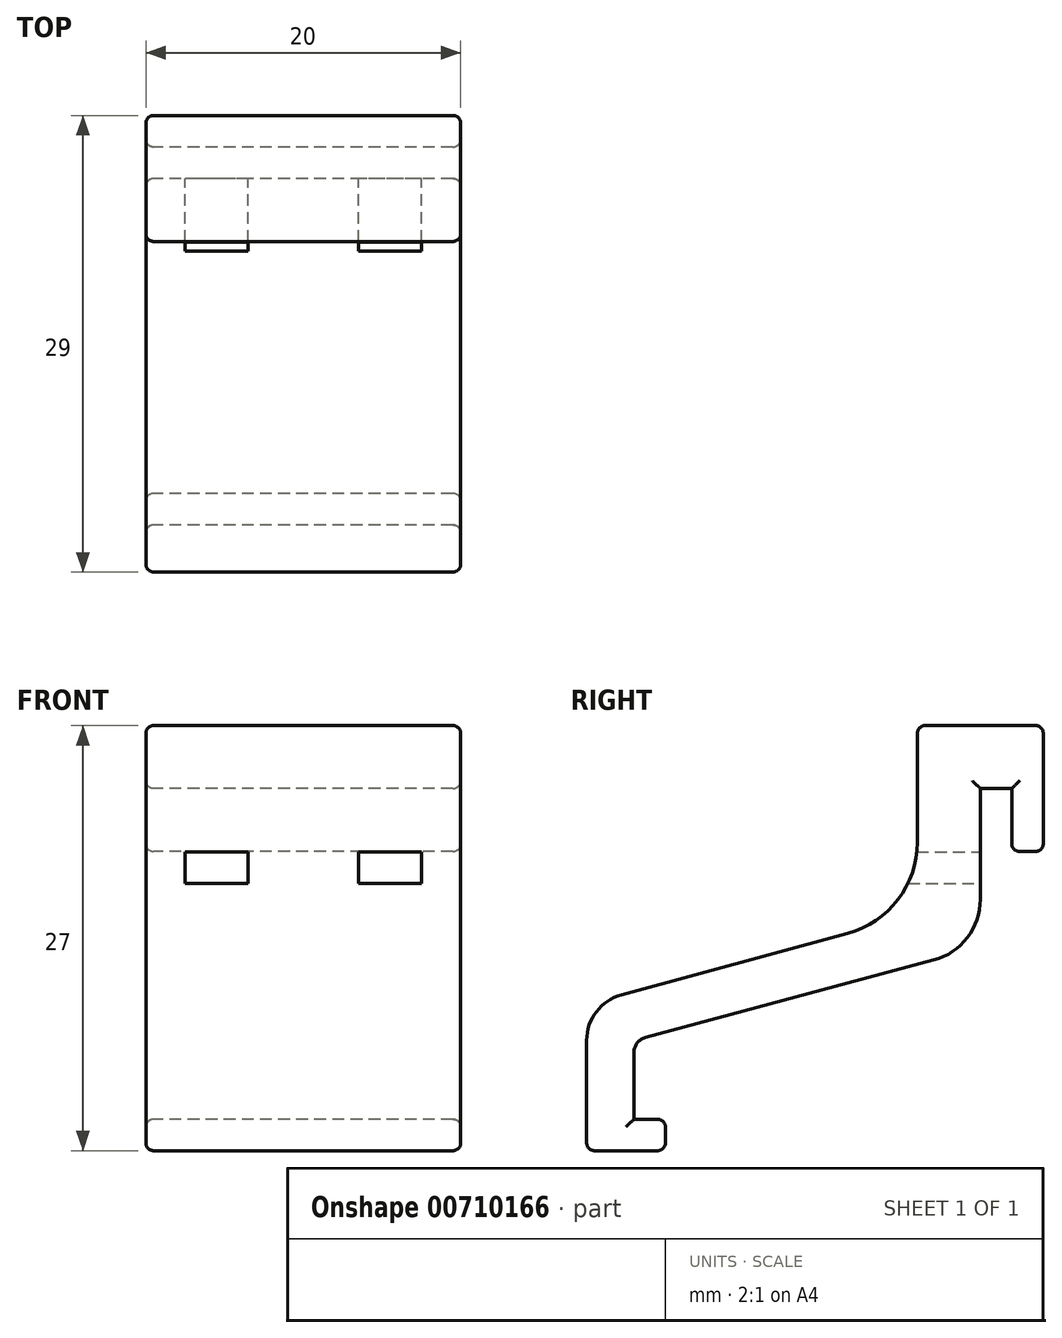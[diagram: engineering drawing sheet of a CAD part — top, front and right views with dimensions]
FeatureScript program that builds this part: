
annotation { "Feature Type Name" : "Feature", "Feature Type Description" : "" }
export const myFeature = defineFeature(function(context is Context, id is Id, definition is map)
    precondition{}
    {
        {
            var Q0;
            Q0=qCreatedBy(makeId("Right.planeOp"),FACE);
            var sketch = newSketch(context, id + "F0", { "sketchPlane" : qUnion([Q0])});
            skLineSegment(sketch, "E0.left", {"start": v(0, 0) * mm, "end": v(0, -7.04) * mm});
            skLineSegment(sketch, "E0.right", {"start": v(-4, 0) * mm, "end": v(-4, -3.41) * mm});
            skLineSegment(sketch, "E1.bottom", {"start": v(0, 0) * mm, "end": v(2, 0) * mm});
            skLineSegment(sketch, "E1.top", {"start": v(-4, 4) * mm, "end": v(4, 4) * mm});
            skLineSegment(sketch, "E1.left", {"start": v(-4, 0) * mm, "end": v(-4, 4) * mm});
            skLineSegment(sketch, "E1.right", {"start": v(4, 0) * mm, "end": v(4, 4) * mm});
            skLineSegment(sketch, "E2.top", {"start": v(4, -4) * mm, "end": v(2, -4) * mm});
            skLineSegment(sketch, "E2.left", {"start": v(4, 0) * mm, "end": v(4, -4) * mm});
            skLineSegment(sketch, "E2.right", {"start": v(2, 0) * mm, "end": v(2, -4) * mm});
            skLineSegment(sketch, "E3", {"start": v(-4, -16) * mm, "end": v(-43.7, -16) * mm, "construction": true});
            skLineSegment(sketch, "E4", {"start": v(-25, 0) * mm, "end": v(-25, -25.14) * mm, "construction": true});
            skLineSegment(sketch, "E5.bottom", {"start": v(-25, -16) * mm, "end": v(-22, -16) * mm});
            skLineSegment(sketch, "E5.left", {"start": v(-25, -16) * mm, "end": v(-25, -21) * mm});
            skLineSegment(sketch, "E5.right", {"start": v(-22, -16.77) * mm, "end": v(-22, -21) * mm});
            skLineSegment(sketch, "E6.bottom", {"start": v(-22, -21) * mm, "end": v(-20, -21) * mm});
            skLineSegment(sketch, "E6.top", {"start": v(-25, -23) * mm, "end": v(-20, -23) * mm});
            skLineSegment(sketch, "E6.left", {"start": v(-25, -21) * mm, "end": v(-25, -23) * mm});
            skLineSegment(sketch, "E6.right", {"start": v(-20, -21) * mm, "end": v(-20, -23) * mm});
            skArc(sketch, "E7", {"start": v(-22.79, -13.1) * mm, "mid": v(-24.38, -14.18) * mm, "end": v(-25, -16) * mm});
            skLineSegment(sketch, "E8", {"start": v(-21.26, -15.8) * mm, "end": v(-2.96, -10.9) * mm});
            skLineSegment(sketch, "E9", {"start": v(-8.43, -9.2) * mm, "end": v(-22.79, -13.1) * mm});
            skPoint(sketch, "E10.orphan", {"position": v(0, -16) * mm});
            skPoint(sketch, "E11.visualSharp", {"position": v(-4, -8) * mm});
            skArc(sketch, "E11.filletArc", {"start": v(-8.43, -9.2) * mm, "mid": v(-5.23, -7.06) * mm, "end": v(-4, -3.41) * mm});
            skPoint(sketch, "E12.visualSharp", {"position": v(0, -10.1) * mm});
            skArc(sketch, "E12.filletArc", {"start": v(-2.96, -10.9) * mm, "mid": v(-0.83, -9.47) * mm, "end": v(0, -7.04) * mm});
            skArc(sketch, "E13.filletArc", {"start": v(-21.26, -15.8) * mm, "mid": v(-21.8, -16.16) * mm, "end": v(-22, -16.77) * mm});
            skSolve(sketch);
        }
        {
            var Q0;
            Q0=makeQuery(id+"F0.imprint","IMPRINT",FACE,{"disambiguationData":[TD([[makeQuery(id+"F0.imprint","IMPRINT",EDGE,{"derivedFrom":sQuery(id+"F0.wireOp",EDGE,"E0.left")}),-1.0]])]});
            extrude(context, id + "F1", {"entities" : qUnion([Q0]), "endBound" : BoundingType.SYMMETRIC, "depth" : 20 * mm, "offsetDistance" : 25 * mm});
        }
        {
            var Q0;
            Q0=makeQuery(id+"F1.opExtrude","SWEPT_FACE",FACE,{"disambiguationData":[OSD([sQuery(id+"F0.wireOp",EDGE,"E0.left")])]});
            var sketch = newSketch(context, id + "F2", { "sketchPlane" : qUnion([Q0])});
            skLineSegment(sketch, "E14.bottom", {"start": v(-7.5, -6.02) * mm, "end": v(-3.5, -6.02) * mm});
            skLineSegment(sketch, "E14.top", {"start": v(-7.5, -4.02) * mm, "end": v(-3.5, -4.02) * mm});
            skLineSegment(sketch, "E14.left", {"start": v(-7.5, -6.02) * mm, "end": v(-7.5, -4.02) * mm});
            skLineSegment(sketch, "E14.right", {"start": v(-3.5, -6.02) * mm, "end": v(-3.5, -4.02) * mm});
            skLineSegment(sketch, "E15.bottom", {"start": v(3.5, -6.02) * mm, "end": v(7.5, -6.02) * mm});
            skLineSegment(sketch, "E15.top", {"start": v(3.5, -4.02) * mm, "end": v(7.5, -4.02) * mm});
            skLineSegment(sketch, "E15.left", {"start": v(3.5, -6.02) * mm, "end": v(3.5, -4.02) * mm});
            skLineSegment(sketch, "E15.right", {"start": v(7.5, -6.02) * mm, "end": v(7.5, -4.02) * mm});
            skSolve(sketch);
        }
        {
            var Q0;
            Q0=makeQuery(id+"F2.imprint","IMPRINT",FACE,{"disambiguationData":[TD([[makeQuery(id+"F2.imprint","IMPRINT",EDGE,{"derivedFrom":sQuery(id+"F2.wireOp",EDGE,"E14.bottom")}),1.0]])]});
            var Q1;
            Q1=makeQuery(id+"F2.imprint","IMPRINT",FACE,{"disambiguationData":[TD([[makeQuery(id+"F2.imprint","IMPRINT",EDGE,{"derivedFrom":sQuery(id+"F2.wireOp",EDGE,"E15.bottom")}),1.0]])]});
            extrude(context, id + "F3", {"entities" : qUnion([Q0, Q1]), "operationType" : NewBodyOperationType.REMOVE, "endBound" : BoundingType.UP_TO_NEXT, "oppositeDirection" : true, "depth" : 25 * mm, "offsetDistance" : 25 * mm});
        }
        {
            var Q0;
            Q0=makeQuery(id+"F1.opExtrude","CAP_EDGE",EDGE,{"disambiguationData":[OSD([sQuery(id+"F0.wireOp",EDGE,"E11.filletArc")])],"isStart":false});
            var Q1;
            Q1=makeQuery(id+"F1.opExtrude","CAP_EDGE",EDGE,{"disambiguationData":[OSD([sQuery(id+"F0.wireOp",EDGE,"E9")])],"isStart":false});
            var Q2;
            Q2=makeQuery(id+"F1.opExtrude","CAP_EDGE",EDGE,{"disambiguationData":[OSD([sQuery(id+"F0.wireOp",EDGE,"E6.top")])],"isStart":false});
            var Q3;
            Q3=makeQuery(id+"F1.opExtrude","CAP_EDGE",EDGE,{"disambiguationData":[OSD([sQuery(id+"F0.wireOp",EDGE,"E6.right")])],"isStart":false});
            var Q4;
            Q4=makeQuery(id+"F1.opExtrude","CAP_EDGE",EDGE,{"disambiguationData":[OSD([sQuery(id+"F0.wireOp",EDGE,"E6.bottom")])],"isStart":false});
            var Q5;
            Q5=makeQuery(id+"F1.opExtrude","CAP_EDGE",EDGE,{"disambiguationData":[OSD([sQuery(id+"F0.wireOp",EDGE,"E5.right")])],"isStart":false});
            var Q6;
            Q6=makeQuery(id+"F1.opExtrude","SWEPT_EDGE",EDGE,{"disambiguationData":[OSD([sQuery(id+"F0.wireOp",EDGE,"E6.top"),sQuery(id+"F0.wireOp",EDGE,"E6.left")])]});
            var Q7;
            Q7=makeQuery(id+"F1.opExtrude","CAP_EDGE",EDGE,{"disambiguationData":[OSD([sQuery(id+"F0.wireOp",EDGE,"E5.left"),sQuery(id+"F0.wireOp",EDGE,"E6.left")])],"isStart":true});
            var Q8;
            Q8=makeQuery(id+"F1.opExtrude","SWEPT_EDGE",EDGE,{"disambiguationData":[OSD([sQuery(id+"F0.wireOp",EDGE,"E1.top"),sQuery(id+"F0.wireOp",EDGE,"E1.left")])]});
            var Q9;
            Q9=makeQuery(id+"F1.opExtrude","CAP_EDGE",EDGE,{"disambiguationData":[OSD([sQuery(id+"F0.wireOp",EDGE,"E1.top")])],"isStart":false});
            var Q10;
            Q10=makeQuery(id+"F1.opExtrude","CAP_EDGE",EDGE,{"disambiguationData":[OSD([sQuery(id+"F0.wireOp",EDGE,"E1.bottom")])],"isStart":false});
            var Q11;
            Q11=makeQuery(id+"F1.opExtrude","CAP_EDGE",EDGE,{"disambiguationData":[OSD([sQuery(id+"F0.wireOp",EDGE,"E2.right")])],"isStart":false});
            var Q12;
            Q12=makeQuery(id+"F1.opExtrude","SWEPT_EDGE",EDGE,{"disambiguationData":[OSD([sQuery(id+"F0.wireOp",EDGE,"E2.top"),sQuery(id+"F0.wireOp",EDGE,"E2.right")])]});
            var Q13;
            Q13=makeQuery(id+"F1.opExtrude","CAP_EDGE",EDGE,{"disambiguationData":[OSD([sQuery(id+"F0.wireOp",EDGE,"E2.top")])],"isStart":false});
            var Q14;
            Q14=makeQuery(id+"F1.opExtrude","CAP_EDGE",EDGE,{"disambiguationData":[OSD([sQuery(id+"F0.wireOp",EDGE,"E1.right"),sQuery(id+"F0.wireOp",EDGE,"E2.left")])],"isStart":false});
            var Q15;
            Q15=makeQuery(id+"F1.opExtrude","SWEPT_EDGE",EDGE,{"disambiguationData":[OSD([sQuery(id+"F0.wireOp",EDGE,"E1.top"),sQuery(id+"F0.wireOp",EDGE,"E1.right")])]});
            var Q16;
            Q16=makeQuery(id+"F1.opExtrude","CAP_EDGE",EDGE,{"disambiguationData":[OSD([sQuery(id+"F0.wireOp",EDGE,"E1.top")])],"isStart":true});
            var Q17;
            Q17=makeQuery(id+"F1.opExtrude","CAP_FACE",FACE,{"disambiguationData":[OSD([sQuery(id+"F0.wireOp",EDGE,"E0.left"),sQuery(id+"F0.wireOp",EDGE,"E0.right"),sQuery(id+"F0.wireOp",EDGE,"E1.bottom"),sQuery(id+"F0.wireOp",EDGE,"E1.top"),sQuery(id+"F0.wireOp",EDGE,"E1.left"),sQuery(id+"F0.wireOp",EDGE,"E1.right"),sQuery(id+"F0.wireOp",EDGE,"E2.top"),sQuery(id+"F0.wireOp",EDGE,"E2.left"),sQuery(id+"F0.wireOp",EDGE,"E2.right"),sQuery(id+"F0.wireOp",EDGE,"E5.left"),sQuery(id+"F0.wireOp",EDGE,"E5.right"),sQuery(id+"F0.wireOp",EDGE,"E6.bottom"),sQuery(id+"F0.wireOp",EDGE,"E6.top"),sQuery(id+"F0.wireOp",EDGE,"E6.left"),sQuery(id+"F0.wireOp",EDGE,"E6.right"),sQuery(id+"F0.wireOp",EDGE,"E7"),sQuery(id+"F0.wireOp",EDGE,"E8"),sQuery(id+"F0.wireOp",EDGE,"E9"),sQuery(id+"F0.wireOp",EDGE,"E11.filletArc"),sQuery(id+"F0.wireOp",EDGE,"E12.filletArc"),sQuery(id+"F0.wireOp",EDGE,"E13.filletArc")])],"isStart":true});
            var Q18;
            Q18=makeQuery(id+"F1.opExtrude","CAP_EDGE",EDGE,{"disambiguationData":[OSD([sQuery(id+"F0.wireOp",EDGE,"E7")])],"isStart":false});
            var Q19;
            Q19=makeQuery(id+"F1.opExtrude","CAP_EDGE",EDGE,{"disambiguationData":[OSD([sQuery(id+"F0.wireOp",EDGE,"E13.filletArc")])],"isStart":false});
            var Q20;
            Q20=makeQuery(id+"F1.opExtrude","SWEPT_EDGE",EDGE,{"disambiguationData":[OSD([sQuery(id+"F0.wireOp",EDGE,"E6.bottom"),sQuery(id+"F0.wireOp",EDGE,"E6.right")])]});
            var Q21;
            Q21=makeQuery(id+"F1.opExtrude","SWEPT_EDGE",EDGE,{"disambiguationData":[OSD([sQuery(id+"F0.wireOp",EDGE,"E6.top"),sQuery(id+"F0.wireOp",EDGE,"E6.right")])]});
            var Q22;
            Q22=makeQuery(id+"F1.opExtrude","SWEPT_EDGE",EDGE,{"disambiguationData":[OSD([sQuery(id+"F0.wireOp",EDGE,"E2.top"),sQuery(id+"F0.wireOp",EDGE,"E2.left")])]});
            fillet(context, id + "F4", {"entities" : qUnion([Q0, Q1, Q2, Q3, Q4, Q5, Q6, Q7, Q8, Q9, Q10, Q11, Q12, Q13, Q14, Q15, Q16, Q17, Q18, Q19, Q20, Q21, Q22]), "tangentPropagation" : true, "radius" : 0.5 * mm, "defaultsChanged" : false, "vertexSettings" : [], "allowEdgeOverflow" : false});
        }
    });
